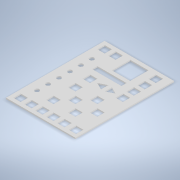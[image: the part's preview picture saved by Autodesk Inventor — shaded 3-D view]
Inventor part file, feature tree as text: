
AUTODESK INVENTOR PART (.ipt)
format: ipt  version: 2021.1 (Build 251245000, 245)  size: 231,424 bytes
history: native  units: mm
features: extrude x1, sketch x1
ambient origin geometry x8: Origin, YZ Plane, XZ Plane, XY Plane, X Axis, Y Axis, Z Axis, Center Point
bodies: Solid1 (feature_tree)
feature tree (2):
  extrude  "Extrusion1"  [1 undecoded]
  sketch  "Sketch1"  dims[d4=3.175mm d5=0.0mm]
note: 1 required parameter value undecoded (feature->parameter linkage not recoverable at this tier; creation-order binding heuristic only, values carry confidence <= 0.55)
